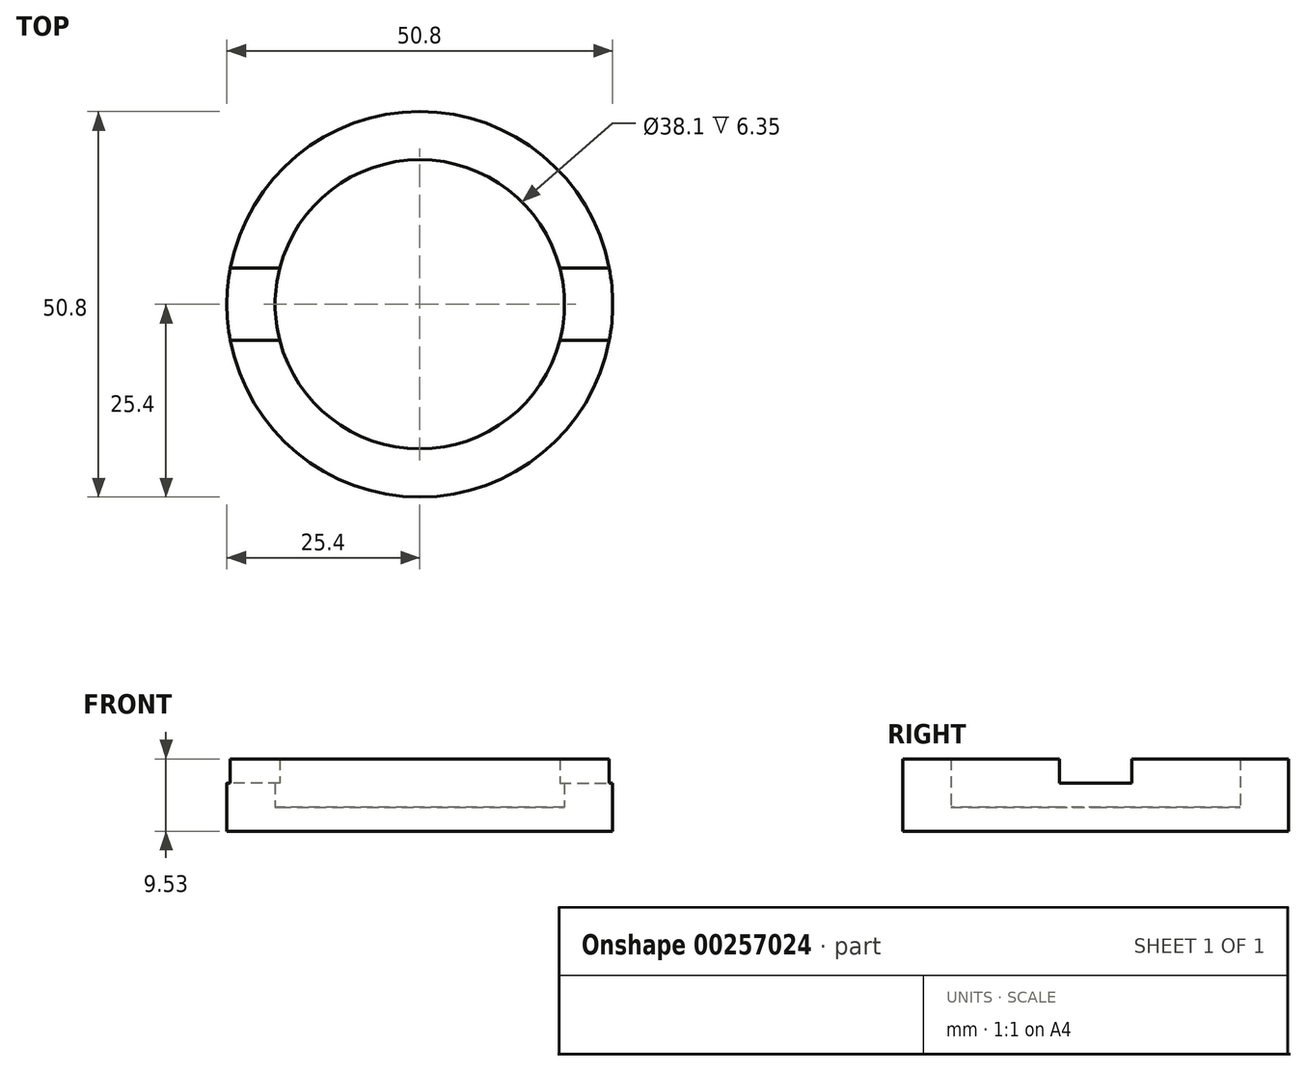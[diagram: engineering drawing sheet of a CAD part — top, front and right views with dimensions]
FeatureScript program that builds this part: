
annotation { "Feature Type Name" : "Feature", "Feature Type Description" : "" }
export const myFeature = defineFeature(function(context is Context, id is Id, definition is map)
    precondition{}
    {
        {
            var Q0;
            Q0=qCreatedBy(makeId("Top.planeOp"),FACE);
            var sketch = newSketch(context, id + "F0", { "sketchPlane" : qUnion([Q0])});
            skCircle(sketch, "E0", {"center": v(0, 0) * mm, "radius": 19.05 * mm});
            skLineSegment(sketch, "E1.bottom", {"start": v(18.45, 4.76) * mm, "end": v(-18.45, 4.76) * mm});
            skLineSegment(sketch, "E1.top", {"start": v(18.45, -4.76) * mm, "end": v(-18.45, -4.76) * mm});
            skLineSegment(sketch, "E1.left", {"start": v(18.45, 4.76) * mm, "end": v(18.45, -4.76) * mm});
            skLineSegment(sketch, "E1.right", {"start": v(-18.45, 4.76) * mm, "end": v(-18.45, -4.76) * mm});
            skLineSegment(sketch, "E2.bottom", {"start": v(25.4, 25.4) * mm, "end": v(-25.4, 25.4) * mm});
            skLineSegment(sketch, "E2.top", {"start": v(25.4, -25.4) * mm, "end": v(-25.4, -25.4) * mm});
            skLineSegment(sketch, "E2.left", {"start": v(25.4, 25.4) * mm, "end": v(25.4, -25.4) * mm});
            skLineSegment(sketch, "E2.right", {"start": v(-25.4, 25.4) * mm, "end": v(-25.4, -25.4) * mm});
            skLineSegment(sketch, "E3.bottom", {"start": v(-18.45, 4.76) * mm, "end": v(-25.4, 4.76) * mm});
            skLineSegment(sketch, "E3.top", {"start": v(-18.45, -4.76) * mm, "end": v(-25.4, -4.76) * mm});
            skLineSegment(sketch, "E3.right", {"start": v(-25.4, 4.76) * mm, "end": v(-25.4, -4.76) * mm});
            skLineSegment(sketch, "E4.bottom", {"start": v(-25.4, 4.76) * mm, "end": v(25.4, 4.76) * mm});
            skLineSegment(sketch, "E4.top", {"start": v(-25.4, -4.76) * mm, "end": v(25.4, -4.76) * mm});
            skLineSegment(sketch, "E4.right", {"start": v(25.4, 4.76) * mm, "end": v(25.4, -4.76) * mm});
            skCircle(sketch, "E5", {"center": v(0, 0) * mm, "radius": 25.4 * mm});
            skSolve(sketch);
        }
        {
            var Q0;
            {var subQ0=sQuery(id+"F0.wireOp",EDGE,"E5");var subQ1=makeQuery(id+"F0.imprint","INTERSECT",VERTEX,{"derivedFrom":[sQuery(id+"F0.wireOp",EDGE,"E2.bottom"),subQ0]});Q0=makeQuery(id+"F0.imprint","IMPRINT",FACE,{"disambiguationData":[TD([[makeQuery(id+"F0.imprint","IMPRINT",EDGE,{"disambiguationData":[TD([[subQ1,1.0]])],"derivedFrom":subQ0}),1.0]])]});}
            var Q1;
            {var subQ0=sQuery(id+"F0.wireOp",EDGE,"E5");var subQ1=makeQuery(id+"F0.imprint","INTERSECT",VERTEX,{"derivedFrom":[sQuery(id+"F0.wireOp",EDGE,"E2.top"),subQ0]});Q1=makeQuery(id+"F0.imprint","IMPRINT",FACE,{"disambiguationData":[TD([[makeQuery(id+"F0.imprint","IMPRINT",EDGE,{"disambiguationData":[TD([[subQ1,1.0]])],"derivedFrom":subQ0}),1.0]])]});}
            extrude(context, id + "F1", {"entities" : qUnion([Q0, Q1]), "depth" : 3.17 * mm});
        }
        {
            var Q0;
            {var subQ0=sQuery(id+"F0.wireOp",EDGE,"E4.bottom");var subQ1=sQuery(id+"F0.wireOp",EDGE,"E0");var subQ2=makeQuery(id+"F0.imprint","INTERSECT",VERTEX,{"derivedFrom":[subQ1,sQuery(id+"F0.wireOp",EDGE,"E1.left"),subQ0]});Q0=makeQuery(id+"F0.imprint","IMPRINT",FACE,{"disambiguationData":[TD([[makeQuery(id+"F0.imprint","IMPRINT",EDGE,{"disambiguationData":[TD([[subQ2,-1.0]])],"derivedFrom":subQ1}),1.0]])]});}
            var Q1;
            {var subQ0=sQuery(id+"F0.wireOp",EDGE,"E5");var subQ1=makeQuery(id+"F0.imprint","INTERSECT",VERTEX,{"derivedFrom":[sQuery(id+"F0.wireOp",EDGE,"E2.bottom"),subQ0]});Q1=makeQuery(id+"F0.imprint","IMPRINT",FACE,{"disambiguationData":[TD([[makeQuery(id+"F0.imprint","IMPRINT",EDGE,{"disambiguationData":[TD([[subQ1,1.0]])],"derivedFrom":subQ0}),1.0]])]});}
            var Q2;
            {var subQ0=sQuery(id+"F0.wireOp",EDGE,"E4.top");var subQ1=sQuery(id+"F0.wireOp",EDGE,"E0");var subQ2=makeQuery(id+"F0.imprint","INTERSECT",VERTEX,{"derivedFrom":[subQ1,sQuery(id+"F0.wireOp",EDGE,"E1.left"),subQ0]});Q2=makeQuery(id+"F0.imprint","IMPRINT",FACE,{"disambiguationData":[TD([[makeQuery(id+"F0.imprint","IMPRINT",EDGE,{"disambiguationData":[TD([[subQ2,1.0]])],"derivedFrom":subQ1}),1.0]])]});}
            var Q3;
            {var subQ0=sQuery(id+"F0.wireOp",EDGE,"E5");var subQ1=makeQuery(id+"F0.imprint","INTERSECT",VERTEX,{"derivedFrom":[sQuery(id+"F0.wireOp",EDGE,"E2.top"),subQ0]});Q3=makeQuery(id+"F0.imprint","IMPRINT",FACE,{"disambiguationData":[TD([[makeQuery(id+"F0.imprint","IMPRINT",EDGE,{"disambiguationData":[TD([[subQ1,1.0]])],"derivedFrom":subQ0}),1.0]])]});}
            var Q4;
            {var subQ4=sQuery(id+"F0.wireOp",EDGE,"E5");var subQ6=makeQuery(id+"F0.imprint","INTERSECT",VERTEX,{"derivedFrom":[sQuery(id+"F0.wireOp",EDGE,"E3.right"),subQ4]});Q4=makeQuery(id+"F0.imprint","IMPRINT",FACE,{"disambiguationData":[TD([[makeQuery(id+"F0.imprint","IMPRINT",EDGE,{"disambiguationData":[TD([[subQ6,1.0]])],"derivedFrom":subQ4}),1.0]])]});}
            var Q5;
            {var subQ4=sQuery(id+"F0.wireOp",EDGE,"E5");var subQ9=makeQuery(id+"F0.imprint","INTERSECT",VERTEX,{"derivedFrom":[sQuery(id+"F0.wireOp",EDGE,"E4.right"),subQ4]});Q5=makeQuery(id+"F0.imprint","IMPRINT",FACE,{"disambiguationData":[TD([[makeQuery(id+"F0.imprint","IMPRINT",EDGE,{"disambiguationData":[TD([[subQ9,-1.0]])],"derivedFrom":subQ4}),1.0]])]});}
            var Q6;
            {var subQ0=sQuery(id+"F0.wireOp",EDGE,"E1.left");Q6=makeQuery(id+"F0.imprint","IMPRINT",FACE,{"disambiguationData":[TD([[makeQuery(id+"F0.imprint","IMPRINT",EDGE,{"derivedFrom":subQ0}),1.0]])]});}
            var Q7;
            {var subQ0=sQuery(id+"F0.wireOp",EDGE,"E1.right");Q7=makeQuery(id+"F0.imprint","IMPRINT",FACE,{"disambiguationData":[TD([[makeQuery(id+"F0.imprint","IMPRINT",EDGE,{"derivedFrom":subQ0}),-1.0]])]});}
            var Q8;
            {var subQ0=sQuery(id+"F0.wireOp",EDGE,"E1.left");Q8=makeQuery(id+"F0.imprint","IMPRINT",FACE,{"disambiguationData":[TD([[makeQuery(id+"F0.imprint","IMPRINT",EDGE,{"derivedFrom":subQ0}),-1.0]])]});}
            extrude(context, id + "F2", {"entities" : qUnion([Q0, Q1, Q2, Q3, Q4, Q5, Q6, Q7, Q8]), "operationType" : NewBodyOperationType.ADD, "oppositeDirection" : true, "depth" : 6.35 * mm});
        }
        {
            var Q0;
            {var subQ0=sQuery(id+"F0.wireOp",EDGE,"E4.bottom");var subQ1=sQuery(id+"F0.wireOp",EDGE,"E0");var subQ2=makeQuery(id+"F0.imprint","INTERSECT",VERTEX,{"derivedFrom":[subQ1,sQuery(id+"F0.wireOp",EDGE,"E1.left"),subQ0]});Q0=makeQuery(id+"F0.imprint","IMPRINT",FACE,{"disambiguationData":[TD([[makeQuery(id+"F0.imprint","IMPRINT",EDGE,{"disambiguationData":[TD([[subQ2,-1.0]])],"derivedFrom":subQ1}),1.0]])]});}
            var Q1;
            {var subQ0=sQuery(id+"F0.wireOp",EDGE,"E1.left");Q1=makeQuery(id+"F0.imprint","IMPRINT",FACE,{"disambiguationData":[TD([[makeQuery(id+"F0.imprint","IMPRINT",EDGE,{"derivedFrom":subQ0}),-1.0]])]});}
            var Q2;
            {var subQ0=sQuery(id+"F0.wireOp",EDGE,"E1.right");Q2=makeQuery(id+"F0.imprint","IMPRINT",FACE,{"disambiguationData":[TD([[makeQuery(id+"F0.imprint","IMPRINT",EDGE,{"derivedFrom":subQ0}),-1.0]])]});}
            var Q3;
            {var subQ0=sQuery(id+"F0.wireOp",EDGE,"E4.top");var subQ1=sQuery(id+"F0.wireOp",EDGE,"E0");var subQ2=makeQuery(id+"F0.imprint","INTERSECT",VERTEX,{"derivedFrom":[subQ1,sQuery(id+"F0.wireOp",EDGE,"E1.left"),subQ0]});Q3=makeQuery(id+"F0.imprint","IMPRINT",FACE,{"disambiguationData":[TD([[makeQuery(id+"F0.imprint","IMPRINT",EDGE,{"disambiguationData":[TD([[subQ2,1.0]])],"derivedFrom":subQ1}),1.0]])]});}
            var Q4;
            {var subQ0=sQuery(id+"F0.wireOp",EDGE,"E1.left");Q4=makeQuery(id+"F0.imprint","IMPRINT",FACE,{"disambiguationData":[TD([[makeQuery(id+"F0.imprint","IMPRINT",EDGE,{"derivedFrom":subQ0}),1.0]])]});}
            extrude(context, id + "F3", {"entities" : qUnion([Q0, Q1, Q2, Q3, Q4]), "operationType" : NewBodyOperationType.REMOVE, "oppositeDirection" : true, "depth" : 3.17 * mm});
        }
    });
